# Revit family: Troffer Light - 2x4 Parabolic
name_source: partatom
category: Lighting Fixtures
revit_build: Autodesk Revit Architecture 2012 (Build: 20110210_1515)
units: mm (PartAtom-declared; Revit-internal decimal feet)

## types (4) — shared parameters
Assembly Code = D5020210
Ballast Number of Poles = 1
Color Filter = 16777215
Diffuser Material = Glass - White, High Luminance
Dimming Lamp Color Temperature Shift = <None>
Emit Shape Visible in Rendering = No
Emit from Rectangle Length = 3' - 10"
Emit from Rectangle Width = 1' - 10"
Grid Material = Metal - Paint Finish - Dark Gray, Matte
Lamp = T-12
Light Box Material = Metal - Chrome
Light Source Symbol Size = 2' - 0"
Load Classification = Lighting - Dwelling Unit

## per-type parameters (varying)
| type | Apparent Load | Ballast Voltage |
| 2'x4'(2 Lamp) - 120V | 80 VA | 120 V |
| 2'x4'(2 Lamp) - 277V | 80 VA | 277 V |
| 2'x4'(4 Lamp) - 120V | 160 VA | 120 V |
| 2'x4'(4 Lamp) - 277V | 160 VA | 277 V |

## geometry (parser evidence)
native form markers: Sweep x1
no freeform markers — native parametric forms only
